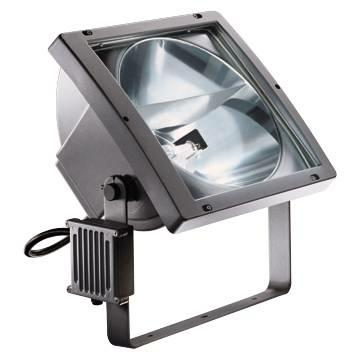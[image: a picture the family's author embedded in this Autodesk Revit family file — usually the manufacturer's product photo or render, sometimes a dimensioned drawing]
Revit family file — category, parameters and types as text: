
# Revit family: Lighting-Proiezione-GEWISS-COLOSSEUM-PROIETTORI_OTTICA_CIRCOLARE
name_source: partatom
category: Apparecchi per illuminazione
units: mm (PartAtom-declared; Revit-internal decimal feet)

## family parameters
Condiviso = No
Host = Superficie
Numero OmniClass = 23.80.70.11.14
Punto di calcolo locali = Sì
Quota connettore circolare = Usa diametro
Sorgente d'illuminazione = No
Taglio con vuoti quando caricato = No
Tipo di parte = Normale
Titolo OmniClass = General Luminaries, Directional

## types (6) — shared parameters
Applicazione = Esterno
Attacco lampada = K12s/Cavo
Carico apparente = 2000 VA
Catalogo = LIGHTING
Catalogo Serie = COLOSSEUM
Certificazione DIN 18032-3 = Conforme
Classe isolamento = I
Classificazione carico = Illuminazione
Codice Electrocod = 2433
Colore = Grigio grafite
Distanza minima dall'oggetto illuminato = 3M
Grado di protezione = IP66
IDF = 5695a8b6-3cb0-4f2f-af48-1678050ede82
IDT = 36e0c751-5da2-4f5b-b782-3005ce20383a
Immagine tipo = GW84656.jpg
Inquinamento luminoso = 0 cd/Klm
L_interna staffa = 515 mm  [stored 1.68963 ft]
Lampada = MN
Lampada: = MN
Manopola di rotazione = <Per categoria>
Materiale = Alluminio
Numero di poli = 2
Ottica = Circolare - ULOR: 0%
Peso (kg) = 16
Peso (kg): = 16
Produttore = GEWISS S.p.A.
Prospetto di default = 1219 mm
Resistenza agli urti = IK09
SEO = Proiettore
Scheda Tecnica = https://www.gewiss.com
Spessore staffa = 40 mm  [stored 0.131234 ft]
Staffa = <Per categoria>
Superficie laterale esposta al vento = 0,083M2
Superficie massima esposta al vento = 0,25M2
URL = https://www.gewiss.com
Versione file RFA = 20.11
Voltaggio = 230 V

## per-type parameters (varying)
| type | Codice EAN | Corrente lampada | Corrente lampada: | Descrizione | Fascio | Modello | Potenza lampada |
| GW84756 - COLOSSEUM CIR. FASCIO DIFF. 1000W MN | 8011564100015 | 9,6 | 9,6A | COLOSSEUM OTTICA CIRCOLARE FASCIO DIFFONDENTE 1000W MN | Diffondente - 20° | GW84756 | 1000W |
| GW84757 - COLOSSEUM CIR. FASCIO DIFF. 2000W MN | 8011564100022 | 11,3A | 11,3A | COLOSSEUM OTTICA CIRCOLARE FASCIO DIFFONDENTE 2000W MN | Diffondente - 20° | GW84757 | 2000W |
| GW84656 - COLOSSEUM CIR. FASCIO CONC. 1000W MN | 8011564065734 | 9,6 | 9,6A | COLOSSEUM OTTICA CIRCOLARE FASCIO CONCENTRANTE 1000W MN | Concentrante - 8° | GW84656 | 1000W |
| GW84754 - COLOSSEUM CIR. FASCIO MEDIO 1000W MN | 8011564099999 | 9,6 | 9,6A | COLOSSEUM OTTICA CIRCOLARE FASCIO MEDIO 1000W MN | Medio - 10° | GW84754 | 1000W |
| GW84755 - COLOSSEUM CIR. FASCIO MEDIO 2000W MN | 8011564100008 | 11,3A | 11,3A | COLOSSEUM OTTICA CIRCOLARE FASCIO MEDIO 2000W MN | Medio - 10° | GW84755 | 2000W |
| GW84657 - COLOSSEUM CIR. FASCIO CONC. 2000W MN | 8011564065765 | 11,3A | 11,3A | COLOSSEUM OTTICA CIRCOLARE FASCIO CONCENTRANTE 2000W MN | Concentrante - 8° | GW84657 | 2000W |

note: [stored X ft] marks values corroborated as IEEE doubles in the binary element streams (Revit-internal decimal feet)
